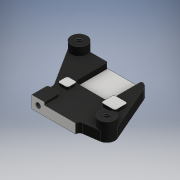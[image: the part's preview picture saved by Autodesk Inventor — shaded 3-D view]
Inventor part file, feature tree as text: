
AUTODESK INVENTOR PART (.ipt)
format: ipt  version: 2018 (Build 220112000, 112)  size: 242,688 bytes
history: native  units: mm
features: extrude x6, sketch x3, projected_geometry x3, hole x2, fillet x1
ambient origin geometry x8: Origin, YZ Plane, XZ Plane, XY Plane, X Axis, Y Axis, Z Axis, Center Point
bodies: Body1 (feature_tree)
feature tree (15):
  sketch  "Sketch7"  dims[d58=7.5mm d60=4.6mm]
  extrude  "Extrusion5"  Depth=4.6mm
  hole  "Hole3"  [1 undecoded]
  extrude  "Extrusion6"  Depth=0.25mm
  extrude  "Extrusion7"  Depth=0.25mm
  extrude  "Extrusion8"  Depth=0.25mm
  extrude  "Extrusion9"  Depth=4.0mm
  extrude  "Extrusion10"  Depth=0.25mm
  hole  "Hole4"  [1 undecoded]
  fillet  "Fillet3"  Radius=9.4mm
  sketch  "Sketch8"  dims[d61=6.3mm d62=3.15mm]
  projected_geometry  "Projected Loop8"
  projected_geometry  "Projected Loop9"
  sketch  "Sketch9"  dims[d63=4.25mm d64=1.95mm d65=1.9mm d66=5.9mm d67=4.0mm d68=19.9mm d69=12.9mm d70=9.4mm d71=9.6mm d72=3.5mm d73=1.0mm d74=0.0mm d75=0.0mm d76=1.567mm d77=4.0mm d78=4.0mm d79=2.0mm d80=90.0deg d81=6.3mm d82=20.594885mm d83=0.5mm d84=2.2mm d85=1.593964mm d86=3.5mm d87=3.25mm d88=4.25mm d89=2.0mm d91=13.1mm d93=5.0mm d94=5.0mm d95=3.5mm d96=0.0mm d97=6.0mm d98=8.5mm d99=1.0mm d100=4.25mm d101=1.4mm d102=0.0mm d103=2.27mm d104=0.0mm d105=0.5mm d106=2.5mm d107=2.15mm d108=0.0mm d109=3.2mm d110=4.0mm d111=2.1mm d112=0.0mm d113=1.221mm d114=3.2mm d115=4.0mm d116=2.0mm d117=90.0deg d118=3.0mm d119=20.594885mm d120=0.25mm]
  projected_geometry  "Projected Loop10"
note: 2 required parameter values undecoded (feature->parameter linkage not recoverable at this tier; creation-order binding heuristic only, values carry confidence <= 0.55)
